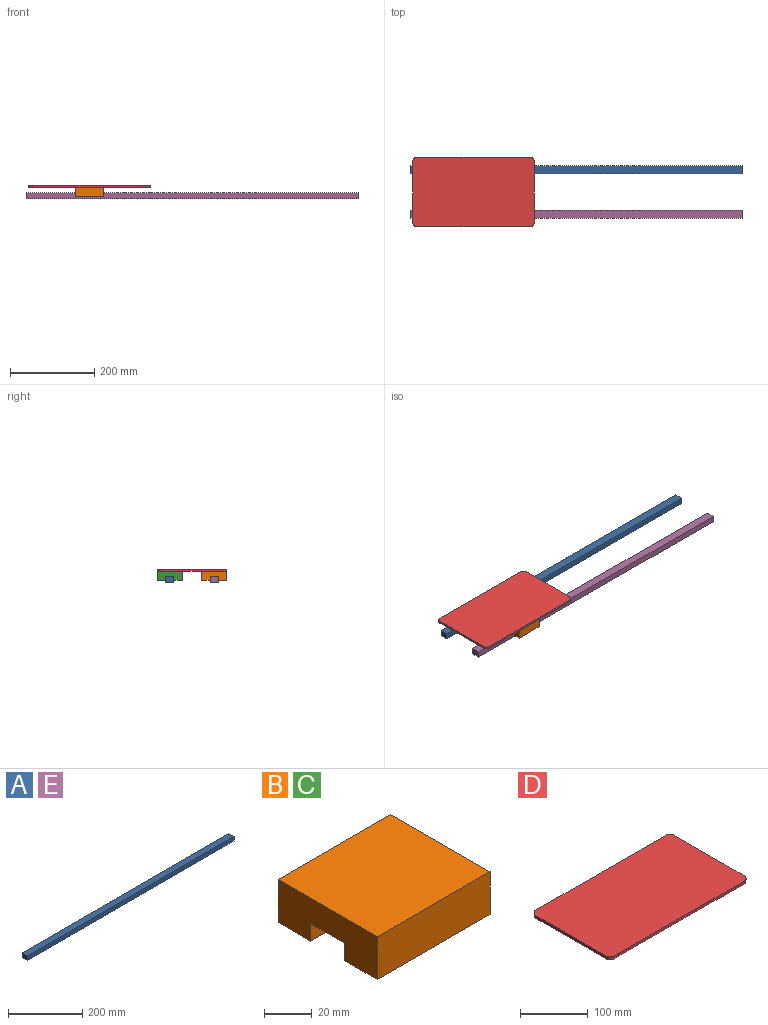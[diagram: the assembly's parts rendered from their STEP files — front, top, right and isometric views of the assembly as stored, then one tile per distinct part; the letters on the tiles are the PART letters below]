
ASSEMBLY  parts=5 mates=5
PART A: 6 faces, bbox 790x20x15 mm
  f0: plane 20x15mm, normal (-1,0,0), area 300mm2, adj f1,f3,f4,f5
  f1: plane 790x15mm, normal (0,-1,0), area 11850mm2, adj f0,f2,f4,f5
  f2: plane 20x15mm, normal (1,0,0), area 300mm2, adj f1,f3,f4,f5
  f3: plane 790x15mm, normal (0,1,0), area 11850mm2, adj f0,f2,f4,f5
  f4: plane 790x20mm, normal (0,0,1), area 15800mm2, adj f0,f1,f2,f3
  f5: plane 790x20mm, normal (0,0,-1), area 15800mm2, adj f0,f1,f2,f3
PART B: 10 faces, bbox 67x59x22 mm
  f0: plane 67x20mm, normal (0,0,-1), area 1340mm2, adj f1,f5,f7,f9
  f1: plane 59x22mm, normal (-1,0,0), area 1118mm2, adj f0,f2,f3,f4,f5,f6,f7,f8
  f2: plane 67x22mm, normal (0,-1,0), area 1474mm2, adj f1,f4,f8,f9
  f3: plane 67x22mm, normal (0,1,0), area 1474mm2, adj f1,f4,f6,f9
  f4: plane 67x59mm, normal (0,0,1), area 3953mm2, adj f1,f2,f3,f9
  f5: plane 67x9mm, normal (0,-1,0), area 603mm2, adj f0,f1,f6,f9
  f6: plane 67x19.5mm, normal (0,0,-1), area 1306.5mm2, adj f1,f3,f5,f9
  f7: plane 67x9mm, normal (0,1,0), area 603mm2, adj f0,f1,f8,f9
  f8: plane 67x19.5mm, normal (0,0,-1), area 1306.5mm2, adj f1,f2,f7,f9
  f9: plane 59x22mm, normal (1,0,0), area 1118mm2, adj f0,f2,f3,f4,f5,f6,f7,f8
PART C: same geometry as B
PART D: 10 faces, bbox 290x165x5 mm
  f0: plane 145x5mm, normal (1,0,0), area 725mm2, adj f3,f4,f5,f6
  f1: plane 270x5mm, normal (0,1,0), area 1350mm2, adj f3,f4,f6,f8
  f2: plane 270x5mm, normal (0,-1,0), area 1350mm2, adj f3,f4,f5,f9
  f3: plane 290x165mm, normal (0,0,1), area 47764.2mm2, adj f0,f1,f2,f5,f6,f7,f8,f9
  f4: plane 290x165mm, normal (0,0,-1), area 47764.2mm2, adj f0,f1,f2,f5,f6,f7,f8,f9
  f5: cylinder r=10mm len=10mm, axis (0,0,1), area 78.5mm2, adj f0,f2,f3,f4
  f6: cylinder r=10mm len=10mm, axis (0,0,-1), area 78.5mm2, adj f0,f1,f3,f4
  f7: plane 145x5mm, normal (-1,0,0), area 725mm2, adj f3,f4,f8,f9
  f8: cylinder r=10mm len=10mm, axis (0,0,1), area 78.5mm2, adj f1,f3,f4,f7
  f9: cylinder r=10mm len=10mm, axis (0,0,-1), area 78.5mm2, adj f2,f3,f4,f7
PART E: same geometry as A
PLACE A t=(0.63,70.5,0.43)mm fixed
PLACE B t=(118.33,-35.5,0.43)mm
PLACE C t=(118.33,70.5,0.43)mm
PLACE D t=(116.83,70.5,0.43)mm
PLACE E t=(0.63,-35.5,0.43)mm
MATE planar A.f0 <-> E.f0  axis (-1,0,0) through (-394.37,70.5,7.93)mm
MATE slider C.f1 <-> A.f0  axis (-1,0,0) through (-276.67,70.5,15.43)mm
MATE slider B.f1 <-> E.f0  axis (-1,0,0) through (-276.67,-35.5,15.43)mm
MATE fastened D.f4 <-> B.f4  axis (0,0,-1) through (-243.17,-65,28.43)mm
MATE fastened C.f4 <-> D.f4  axis (0,0,1) through (-243.17,100,28.43)mm
